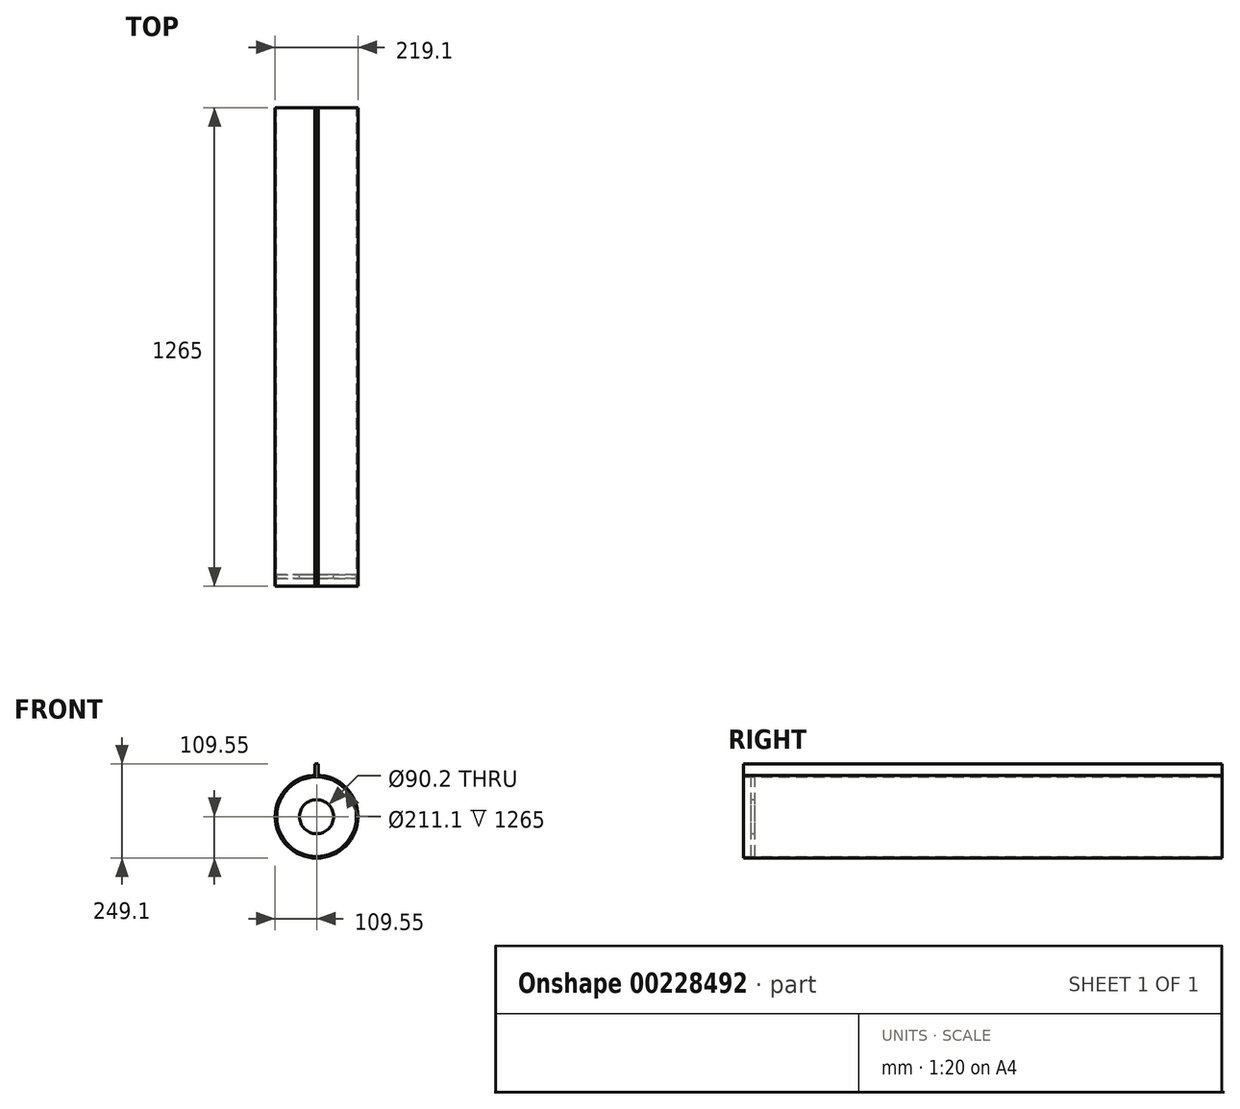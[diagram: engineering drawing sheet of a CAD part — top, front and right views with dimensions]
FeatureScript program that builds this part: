
annotation { "Feature Type Name" : "Feature", "Feature Type Description" : "" }
export const myFeature = defineFeature(function(context is Context, id is Id, definition is map)
    precondition{}
    {
        {
            assignVariable(context, id + "F0", {"name" : "L", "anyValue" : 1265});
        }
        {
            var Q0;
            Q0=qCreatedBy(makeId("Front.planeOp"),FACE);
            var sketch = newSketch(context, id + "F1", { "sketchPlane" : qUnion([Q0])});
            skCircle(sketch, "E0", {"center": v(0, 0) * mm, "radius": 45.1 * mm});
            skCircle(sketch, "E1", {"center": v(0, 0) * mm, "radius": 109.55 * mm});
            skCircle(sketch, "E2.0", {"center": v(0, 0) * mm, "radius": 105.55 * mm});
            skLineSegment(sketch, "E3.bottom", {"start": v(-5, 139.55) * mm, "end": v(5, 139.55) * mm});
            skLineSegment(sketch, "E3.top", {"start": v(-5, 109.55) * mm, "end": v(5, 109.55) * mm});
            skLineSegment(sketch, "E3.left", {"start": v(-5, 139.55) * mm, "end": v(-5, 109.55) * mm});
            skLineSegment(sketch, "E3.right", {"start": v(5, 139.55) * mm, "end": v(5, 109.55) * mm});
            skPoint(sketch, "E3.middle", {"position": v(0, 124.55) * mm});
            skCircle(sketch, "E4", {"center": v(0, 0) * mm, "radius": 105.25 * mm});
            skSolve(sketch);
        }
        {
            var Q0;
            Q0=makeQuery(id+"F1.imprint","IMPRINT",FACE,{"disambiguationData":[TD([[makeQuery(id+"F1.imprint","IMPRINT",EDGE,{"derivedFrom":sQuery(id+"F1.wireOp",EDGE,"E1")}),1.0]])]});
            extrude(context, id + "F2", {"entities" : qUnion([Q0]), "depth" : (getVariable(context, 'L')) * mm, "hasSecondDirection" : true, "secondDirectionOppositeDirection" : true, "secondDirectionDepth" : 25 * mm, "symmetric" : true});
        }
        {
            var Q0;
            Q0=makeQuery(id+"F1.imprint","IMPRINT",FACE,{"disambiguationData":[TD([[makeQuery(id+"F1.imprint","IMPRINT",EDGE,{"derivedFrom":sQuery(id+"F1.wireOp",EDGE,"E0")}),-1.0]])]});
            var Q1;
            Q1=makeQuery(id+"F2.opExtrude","CAP_FACE",FACE,{"disambiguationData":[OSD([sQuery(id+"F1.wireOp",EDGE,"E1"),sQuery(id+"F1.wireOp",EDGE,"E4")])],"isStart":false});
            var Q2;
            Q2=makeQuery(id+"F2.opExtrude","CAP_FACE",FACE,{"disambiguationData":[OSD([sQuery(id+"F1.wireOp",EDGE,"E1"),sQuery(id+"F1.wireOp",EDGE,"E4")])],"isStart":false});
            extrude(context, id + "F3", {"entities" : qUnion([Q0]), "endBound" : BoundingType.UP_TO_SURFACE, "endBoundEntityFace" : qUnion([Q1]), "depth" : (getVariable(context, 'L') / 2 - 20) * mm, "hasSecondDirection" : true, "secondDirectionBound" : BoundingType.UP_TO_SURFACE, "secondDirectionOppositeDirection" : false, "secondDirectionBoundEntityFace" : qUnion([Q2]), "secondDirectionDepth" : (getVariable(context, 'L') / 2 - 30) * mm, "hasOffset" : true, "offsetDistance" : 20 * mm, "hasSecondDirectionOffset" : true, "secondDirectionOffsetDistance" : 30 * mm});
        }
        {
            var Q0;
            Q0=makeQuery(id+"F1.imprint","IMPRINT",FACE,{"disambiguationData":[TD([[makeQuery(id+"F1.imprint","IMPRINT",EDGE,{"derivedFrom":sQuery(id+"F1.wireOp",EDGE,"E3.bottom")}),-1.0]])]});
            var Q1;
            Q1=makeQuery(id+"F2.opExtrude","CAP_FACE",FACE,{"disambiguationData":[OSD([sQuery(id+"F1.wireOp",EDGE,"E1"),sQuery(id+"F1.wireOp",EDGE,"E2.0")])],"isStart":false});
            var Q2;
            Q2=makeQuery(id+"F2.opExtrude","CAP_FACE",FACE,{"disambiguationData":[OSD([sQuery(id+"F1.wireOp",EDGE,"E1"),sQuery(id+"F1.wireOp",EDGE,"E2.0")])],"isStart":true});
            extrude(context, id + "F4", {"entities" : qUnion([Q0]), "endBound" : BoundingType.UP_TO_SURFACE, "endBoundEntityFace" : qUnion([Q1]), "depth" : 1500 * mm, "hasSecondDirection" : true, "secondDirectionBound" : BoundingType.UP_TO_SURFACE, "secondDirectionOppositeDirection" : true, "secondDirectionBoundEntityFace" : qUnion([Q2]), "secondDirectionDepth" : 25 * mm});
        }
    });
